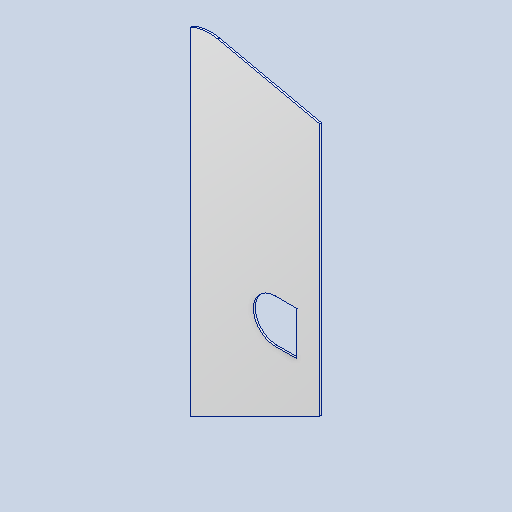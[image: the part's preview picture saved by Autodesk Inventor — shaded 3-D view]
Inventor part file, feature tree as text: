
AUTODESK INVENTOR PART (.ipt)
format: ipt  version: 2023 (Build 270158000, 158)  size: 112,128 bytes
history: native  units: mm
features: other x4, extrude x2, sketch x2, reference x2, projected_geometry x1
ambient origin geometry x8: Origin, YZ Plane, XZ Plane, XY Plane, X Axis, Y Axis, Z Axis, Center Point
bodies: Solid1 (feature_tree)
feature tree (11):
  extrude  "Extrusion1"  Depth=10.0mm TaperAngle=0.0deg
  extrude  "Extrusion2"  [1 undecoded]
  sketch  "Sketch1"  dims[d0=0.5mm d1=0.0mm d2=10.0mm d3=0.0mm]
  reference  "Reference1"
  sketch  "Sketch2"
  reference  "Reference2"
  projected_geometry  "Projected Loop1"
  other  "<userpath>\Desktop\MojeRoboty\Stefan\mechanics\zlozenie.iam"
  other  "zlozenie.iam"
  other  "pokrywa lewa:1"
  other  "sciana_prawa_v4:1"
note: 1 required parameter value undecoded (feature->parameter linkage not recoverable at this tier; creation-order binding heuristic only, values carry confidence <= 0.55)
